# Revit family: Storage-Frestanding-Teknion-BSMLF_Mid_Height_Credenza_Open_and_Drawers-R2018
name_source: partatom
category: Furniture
revit_build: Autodesk Revit 2018 (Build: 20190510_1515(x64)
units: mm (PartAtom-declared; Revit-internal decimal feet)

## family parameters
Always vertical = Yes
Cut with Voids When Loaded = No
OmniClass Number = 23.40.20.00
OmniClass Title = General Furniture and Specialties
Room Calculation Point = No
Shared = Yes
Work Plane-Based = No

## types (2) — shared parameters
Assembly Code = E2020200
Manufacturer = Teknion
Manufacturer Fax = 416.661.4586
Part Number = BSMLF
Product Documentation Link = https://www.teknion.com
Product Line = Expansion Casegoods
Product Page URL = https://www.teknion.com
Series = Expansion Casegoods
Sustainability Data = https://www.teknion.com
URL = www.teknion.com
Unit Weight URL = http://www.teknion.com
Warranty = http://www.teknion.com

## per-type parameters (varying)
| type | Description | Left Cut | Model | Right Cut |
| Left Drawer Configuration | Mid-Height Credenza - Open and Drawers, 18" Depth, 21" Height, Left Drawer Configuration | Yes | BSMLF18__21L | No |
| Right Drawer Configuration | Mid-Height Credenza - Open and Drawers, 18" Depth, 21" Height, Right Drawer Configuration | No | BSMLF18__21R | Yes |

## geometry (parser evidence)
native form markers: Sweep x2
no freeform markers — native parametric forms only
